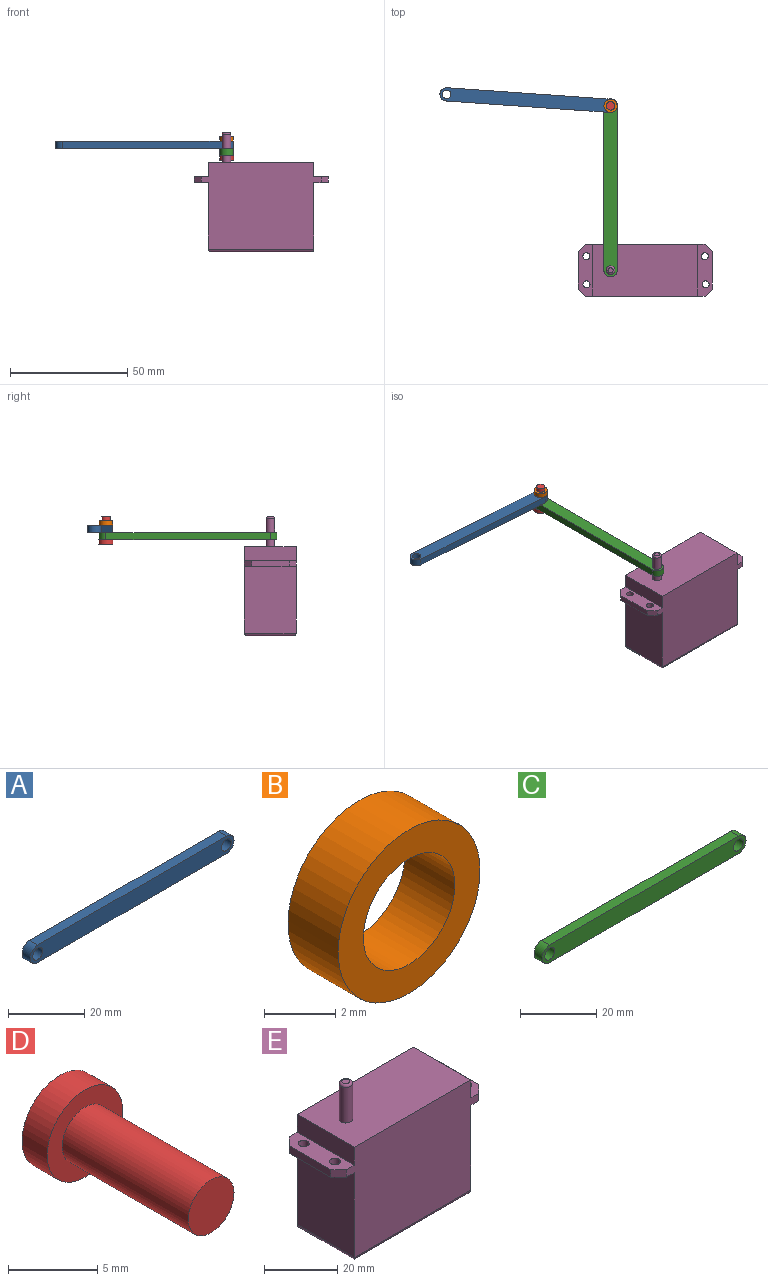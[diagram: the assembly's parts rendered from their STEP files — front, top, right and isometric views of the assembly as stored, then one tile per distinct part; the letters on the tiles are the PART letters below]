
ASSEMBLY  parts=5 mates=4
PART A: 8 faces, bbox 75.7x3x5.7 mm
  f0: cylinder r=2.82mm len=5.65mm, axis (0,1,0), area 26.6mm2, adj f1,f3,f6,f7
  f1: plane 70x3mm, normal (0,0,-1), area 210mm2, adj f0,f2,f6,f7
  f2: cylinder r=2.82mm len=5.65mm, axis (0,1,0), area 26.6mm2, adj f1,f3,f6,f7
  f3: plane 70x3mm, normal (0,0,1), area 210mm2, adj f0,f2,f6,f7
  f4: cylinder r=1.82mm len=3.65mm, axis (0,1,0), area 34.4mm2, adj f6,f7
  f5: cylinder r=1.82mm len=3.65mm, axis (0,1,0), area 34.4mm2, adj f6,f7
  f6: plane 75.65x5.65mm, normal (0,-1,0), area 399.6mm2, adj f0,f1,f2,f3,f4,f5
  f7: plane 75.65x5.65mm, normal (0,1,0), area 399.6mm2, adj f0,f1,f2,f3,f4,f5
PART B: 4 faces, bbox 5.7x2x5.7 mm
  f0: cylinder r=1.82mm len=3.65mm, axis (0,1,0), area 22.9mm2, adj f2,f3
  f1: cylinder r=2.82mm len=5.65mm, axis (0,1,0), area 35.5mm2, adj f2,f3
  f2: plane 5.65x5.65mm, normal (0,-1,0), area 14.6mm2, adj f0,f1
  f3: plane 5.65x5.65mm, normal (0,1,0), area 14.6mm2, adj f0,f1
PART C: 8 faces, bbox 75.7x3x5.7 mm
  f0: cylinder r=2.82mm len=5.65mm, axis (0,1,0), area 26.6mm2, adj f1,f3,f6,f7
  f1: plane 70x3mm, normal (0,0,-1), area 210mm2, adj f0,f2,f6,f7
  f2: cylinder r=2.82mm len=5.65mm, axis (0,1,0), area 26.6mm2, adj f1,f3,f6,f7
  f3: plane 70x3mm, normal (0,0,1), area 210mm2, adj f0,f2,f6,f7
  f4: cylinder r=1.82mm len=3.65mm, axis (0,1,0), area 34.4mm2, adj f6,f7
  f5: cylinder r=1.82mm len=3.65mm, axis (0,1,0), area 34.4mm2, adj f6,f7
  f6: plane 75.65x5.65mm, normal (0,-1,0), area 399.6mm2, adj f0,f1,f2,f3,f4,f5
  f7: plane 75.65x5.65mm, normal (0,1,0), area 399.6mm2, adj f0,f1,f2,f3,f4,f5
PART D: 5 faces, bbox 6x12x6 mm
  f0: cylinder r=1.81mm len=10mm, axis (0,1,0), area 114mm2, adj f1,f3
  f1: plane 3.63x3.63mm, normal (0,-1,0), area 10.3mm2, adj f0
  f2: cylinder r=3mm len=6mm, axis (0,1,0), area 37.7mm2, adj f3,f4
  f3: plane 6x6mm, normal (0,-1,0), area 17.9mm2, adj f0,f2
  f4: plane 6x6mm, normal (0,1,0), area 28.3mm2, adj f2
PART E: 29 faces, bbox 57x22x50.6 mm
  f0: plane 22x6.01mm, normal (1,0,0), area 132.1mm2, adj f1,f11,f12,f13
  f1: plane 45x22mm, normal (0,0,1), area 979.6mm2, adj f0,f2,f12,f13,f22
  f2: plane 22x6.01mm, normal (-1,0,0), area 132.1mm2, adj f1,f3,f12,f13
  f3: plane 22x6mm, normal (0,0,1), area 108.9mm2, adj f2,f4,f12,f13,f16,f17,f20,f21
  f4: plane 16x2.5mm, normal (-1,0,0), area 40mm2, adj f3,f5,f16,f17
  f5: plane 22x6mm, normal (0,0,-1), area 108.9mm2, adj f4,f6,f12,f13,f16,f17,f20,f21
  f6: plane 28.36x22mm, normal (-1,0,0), area 623.9mm2, adj f5,f12,f13,f28
  f7: plane 42.73x19.73mm, normal (0,0,-1), area 843.1mm2, adj f25,f26,f27,f28
  f8: plane 28.36x22mm, normal (1,0,0), area 623.9mm2, adj f9,f12,f13,f25
  f9: plane 22x6mm, normal (0,0,-1), area 108.9mm2, adj f8,f10,f12,f13,f14,f15,f18,f19
  f10: plane 16x2.5mm, normal (1,0,0), area 40mm2, adj f9,f11,f14,f15
  f11: plane 22x6mm, normal (0,0,1), area 108.9mm2, adj f0,f10,f12,f13,f14,f15,f18,f19
  f12: plane 51x36.87mm, normal (0,-1,0), area 1673.9mm2, adj f0,f1,f2,f3,f5,f6,f8,f9
  f13: plane 51x36.87mm, normal (0,1,0), area 1673.9mm2, adj f0,f1,f2,f3,f5,f6,f8,f9
  f14: plane 3x3mm, normal (0.71,0.71,0), area 10.6mm2, adj f9,f10,f11,f13
  f15: plane 3x3mm, normal (0.71,-0.71,0), area 10.6mm2, adj f9,f10,f11,f12
  f16: plane 3x3mm, normal (-0.71,0.71,0), area 10.6mm2, adj f3,f4,f5,f13
  f17: plane 3x3mm, normal (-0.71,-0.71,0), area 10.6mm2, adj f3,f4,f5,f12
  f18: cylinder r=1.5mm len=3mm, axis (0,0,1), area 23.6mm2, adj f9,f11
  f19: cylinder r=1.5mm len=3mm, axis (0,0,1), area 23.6mm2, adj f9,f11
  f20: cylinder r=1.5mm len=3mm, axis (0,0,1), area 23.6mm2, adj f3,f5
  f21: cylinder r=1.5mm len=3mm, axis (0,0,1), area 23.6mm2, adj f3,f5
  f22: cylinder r=1.82mm len=11.88mm, axis (0,0,-1), area 135.9mm2, adj f1,f24
  f23: plane 2.19x2.19mm, normal (0,0,1), area 3.8mm2, adj f24
  f24: torus R=1.1mm, axis (0,0,1), area 11.1mm2, adj f22,f23
  f25: cylinder r=1.13mm len=22mm, axis (0,-1,0), area 37.7mm2, adj f7,f8,f26,f27
  f26: cylinder r=1.13mm len=45mm, axis (-1,0,0), area 78.7mm2, adj f7,f12,f25,f28
  f27: cylinder r=1.13mm len=45mm, axis (1,0,0), area 78.7mm2, adj f7,f13,f25,f28
  f28: cylinder r=1.13mm len=22mm, axis (0,1,0), area 37.7mm2, adj f6,f7,f26,f27
PLACE A rot(axis=(-0.02,-0.71,0.71),177.2deg) t=(117.63,58.25,57.4)mm
PLACE B rot(axis=(-1,0,0),90deg) t=(123.63,57.83,60.52)mm
PLACE C rot(axis=(-0.58,-0.58,0.58),120deg) t=(123.63,48.6,54.33)mm
PLACE D rot(axis=(-1,0,0),90deg) t=(123.63,57.83,52.26)mm
PLACE E t=(126.54,-1.17,0)mm
MATE cylindrical A.f0 <-> D.f0  axis (0,0,-1) through (123.63,57.83,60.4)mm
MATE cylindrical C.f0 <-> E.f22  axis (0,0,-1) through (123.63,-12.17,57.33)mm
MATE cylindrical D.f0 <-> C.f2  axis (0,0,-1) through (123.63,57.83,59.26)mm
MATE cylindrical B.f0 <-> D.f0  axis (0,0,-1) through (123.63,57.83,62.52)mm
